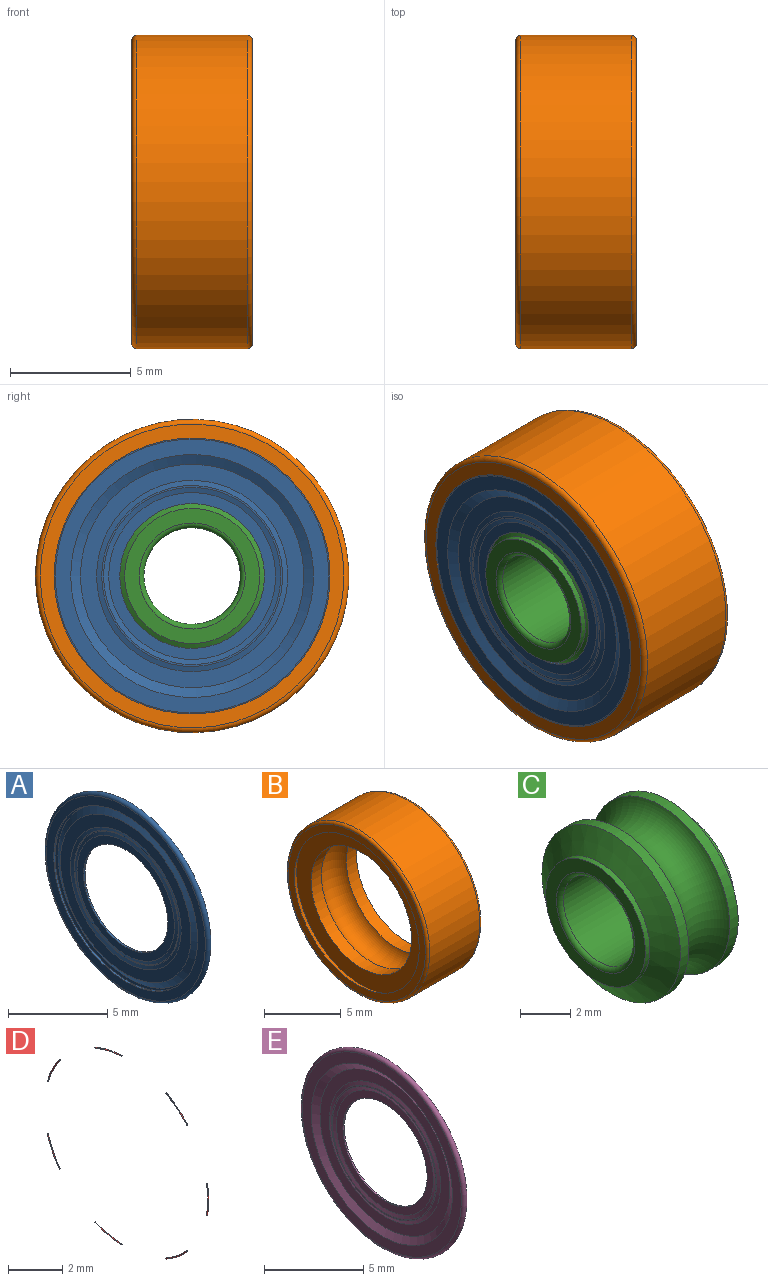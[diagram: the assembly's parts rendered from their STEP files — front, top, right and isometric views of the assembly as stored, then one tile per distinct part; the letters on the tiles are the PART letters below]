
ASSEMBLY  parts=5 mates=5
PART A: 20 faces, bbox 0.3x12.7x12.7 mm
  f0: torus R=5.68mm, axis (1,0,0), area 19mm2, adj f12,f13
  f1: torus R=5.68mm, axis (1,0,0), area 7.5mm2, adj f10,f11
  f2: cone r=3.84mm half-angle=72.7deg, axis (-1,0,0), area 5.4mm2, adj f18,f19
  f3: cone r=3.58mm half-angle=72.7deg, axis (1,0,0), area 5mm2, adj f17,f18
  f4: cylinder r=3mm len=6.01mm, axis (1,0,0), area 1.9mm2, adj f16,f17
  f5: cone r=3.57mm half-angle=72.7deg, axis (1,0,0), area 5mm2, adj f15,f16
  f6: cone r=3.86mm half-angle=72.7deg, axis (-1,0,0), area 5.4mm2, adj f14,f15
  f7: cone r=4.84mm half-angle=60deg, axis (1,0,0), area 14.2mm2, adj f13,f14
  f8: cylinder r=5.13mm len=10.27mm, axis (1,0,0), area 3.2mm2, adj f11,f12
  f9: cone r=4.86mm half-angle=60deg, axis (1,0,0), area 14.3mm2, adj f10,f19
  f10: plane 11.35x11.35mm, normal (-1,0,0), area 20.7mm2, adj f1,f9
  f11: plane 11.35x11.35mm, normal (1,0,0), area 18.5mm2, adj f1,f8
  f12: plane 11.35x11.35mm, normal (-1,0,0), area 18.5mm2, adj f0,f8
  f13: plane 11.35x11.35mm, normal (1,0,0), area 21.5mm2, adj f0,f7
  f14: plane 9.27x9.27mm, normal (1,0,0), area 18.1mm2, adj f6,f7
  f15: plane 7.5x7.5mm, normal (1,0,0), area 1.8mm2, adj f5,f6
  f16: plane 6.92x6.92mm, normal (1,0,0), area 9.3mm2, adj f4,f5
  f17: plane 6.95x6.95mm, normal (-1,0,0), area 9.6mm2, adj f3,f4
  f18: plane 7.47x7.47mm, normal (-1,0,0), area 1.1mm2, adj f2,f3
  f19: plane 9.32x9.32mm, normal (-1,0,0), area 19.2mm2, adj f2,f9
PART B: 12 faces, bbox 5x14.1x14.1 mm
  f0: torus R=4.25mm, axis (1,0,0), area 98.4mm2, adj f6,f7
  f1: cone r=5.85mm half-angle=30deg, axis (-1,0,0), area 17.7mm2, adj f10,f11
  f2: torus R=6.3mm, axis (1,0,0), area 12.7mm2, adj f3,f10
  f3: cylinder r=6.5mm len=13mm, axis (1,0,0), area 187.9mm2, adj f2,f4
  f4: torus R=6.3mm, axis (1,0,0), area 12.7mm2, adj f3,f9
  f5: cone r=5.85mm half-angle=30deg, axis (1,0,0), area 17.7mm2, adj f8,f9
  f6: cylinder r=4.61mm len=9.22mm, axis (1,0,0), area 27.2mm2, adj f0,f8
  f7: cylinder r=4.61mm len=9.22mm, axis (1,0,0), area 27.2mm2, adj f0,f11
  f8: plane 11.93x11.93mm, normal (-1,0,0), area 45mm2, adj f5,f6
  f9: plane 12.6x12.6mm, normal (-1,0,0), area 21.7mm2, adj f4,f5
  f10: plane 12.6x12.6mm, normal (1,0,0), area 21.7mm2, adj f1,f2
  f11: plane 11.93x11.93mm, normal (1,0,0), area 45mm2, adj f1,f7
PART C: 12 faces, bbox 5x9.2x9.2 mm
  f0: torus R=4.25mm, axis (1,0,0), area 63.9mm2, adj f5,f6
  f1: cylinder r=2mm len=4.6mm, axis (1,0,0), area 57.8mm2, adj f2,f9
  f2: torus R=2.2mm, axis (1,0,0), area 4.1mm2, adj f1,f11
  f3: cylinder r=2.8mm len=5.6mm, axis (1,0,0), area 4.4mm2, adj f4,f11
  f4: cone r=3.34mm half-angle=60deg, axis (-1,0,0), area 26.5mm2, adj f3,f5
  f5: cylinder r=3.89mm len=7.78mm, axis (1,0,0), area 11.6mm2, adj f0,f4
  f6: cylinder r=3.89mm len=7.78mm, axis (1,0,0), area 11.6mm2, adj f0,f7
  f7: cone r=3.34mm half-angle=60deg, axis (1,0,0), area 26.5mm2, adj f6,f8
  f8: cylinder r=2.8mm len=5.6mm, axis (1,0,0), area 4.4mm2, adj f7,f10
  f9: torus R=2.2mm, axis (1,0,0), area 4.1mm2, adj f1,f10
  f10: plane 5.6x5.6mm, normal (-1,0,0), area 9.4mm2, adj f8,f9
  f11: plane 5.6x5.6mm, normal (1,0,0), area 9.4mm2, adj f2,f3
PART D: 21 faces, bbox 0x8.5x8.6 mm
  f0: torus R=4.25mm, axis (1,0,0), area 0.2mm2, adj f1,f2
  f1: sphere r=1.2mm, area 0mm2, adj f0
  f2: sphere r=1.2mm, area 0mm2, adj f0
  f3: torus R=4.25mm, axis (1,0,0), area 0.2mm2, adj f4,f5
  f4: sphere r=1.2mm, area 0mm2, adj f3
  f5: sphere r=1.2mm, area 0mm2, adj f3
  f6: torus R=4.25mm, axis (1,0,0), area 0.2mm2, adj f7,f8
  f7: sphere r=1.2mm, area 0mm2, adj f6
  f8: sphere r=1.2mm, area 0mm2, adj f6
  f9: torus R=4.25mm, axis (1,0,0), area 0.2mm2, adj f10,f11
  f10: sphere r=1.2mm, area 0mm2, adj f9
  f11: sphere r=1.2mm, area 0mm2, adj f9
  f12: torus R=4.25mm, axis (1,0,0), area 0.2mm2, adj f13,f14
  f13: sphere r=1.2mm, area 0mm2, adj f12
  f14: sphere r=1.2mm, area 0mm2, adj f12
  f15: torus R=4.25mm, axis (1,0,0), area 0.2mm2, adj f16,f17
  f16: sphere r=1.2mm, area 0mm2, adj f15
  f17: sphere r=1.2mm, area 0mm2, adj f15
  f18: torus R=4.25mm, axis (1,0,0), area 0.2mm2, adj f19,f20
  f19: sphere r=1.2mm, area 0mm2, adj f18
  f20: sphere r=1.2mm, area 0mm2, adj f18
PART E: 20 faces, bbox 0.3x12.7x12.7 mm
  f0: torus R=5.68mm, axis (-1,0,0), area 19mm2, adj f12,f13
  f1: torus R=5.68mm, axis (-1,0,0), area 7.5mm2, adj f10,f11
  f2: cone r=3.84mm half-angle=72.7deg, axis (1,0,0), area 5.4mm2, adj f18,f19
  f3: cone r=3.58mm half-angle=72.7deg, axis (-1,0,0), area 5mm2, adj f17,f18
  f4: cylinder r=3mm len=6.01mm, axis (-1,0,0), area 1.9mm2, adj f16,f17
  f5: cone r=3.57mm half-angle=72.7deg, axis (-1,0,0), area 5mm2, adj f15,f16
  f6: cone r=3.86mm half-angle=72.7deg, axis (1,0,0), area 5.4mm2, adj f14,f15
  f7: cone r=4.84mm half-angle=60deg, axis (-1,0,0), area 14.2mm2, adj f13,f14
  f8: cylinder r=5.13mm len=10.27mm, axis (-1,0,0), area 3.2mm2, adj f11,f12
  f9: cone r=4.86mm half-angle=60deg, axis (-1,0,0), area 14.3mm2, adj f10,f19
  f10: plane 11.35x11.35mm, normal (1,0,0), area 20.7mm2, adj f1,f9
  f11: plane 11.35x11.35mm, normal (-1,0,0), area 18.5mm2, adj f1,f8
  f12: plane 11.35x11.35mm, normal (1,0,0), area 18.5mm2, adj f0,f8
  f13: plane 11.35x11.35mm, normal (-1,0,0), area 21.5mm2, adj f0,f7
  f14: plane 9.27x9.27mm, normal (-1,0,0), area 18.1mm2, adj f6,f7
  f15: plane 7.5x7.5mm, normal (-1,0,0), area 1.8mm2, adj f5,f6
  f16: plane 6.92x6.92mm, normal (-1,0,0), area 9.3mm2, adj f4,f5
  f17: plane 6.95x6.95mm, normal (1,0,0), area 9.6mm2, adj f3,f4
  f18: plane 7.47x7.47mm, normal (1,0,0), area 1.1mm2, adj f2,f3
  f19: plane 9.32x9.32mm, normal (1,0,0), area 19.2mm2, adj f2,f9
PLACE A rot(axis=(0,1,0),180deg) t=(1.61,8,2.83)mm
PLACE B t=(1.19,8,2.83)mm
PLACE C t=(1.19,8,2.83)mm
PLACE D t=(1.19,8,2.83)mm
PLACE E t=(1.27,8,2.83)mm
MATE revolute C.f0 <-> B.f0  axis (1,0,0) through (3.69,8,2.83)mm
MATE revolute A.f0 <-> C.f0  axis (-1,0,0) through (1.19,8,2.83)mm
MATE planar C.f0 <-> B.f0  axis (1,0,0) through (3.69,8,2.83)mm
MATE revolute E.f5 <-> C.f0  axis (1,0,0) through (6.19,8,2.83)mm
MATE revolute D.f0 <-> C.f0  axis (1,0,0) through (3.69,8,2.83)mm
